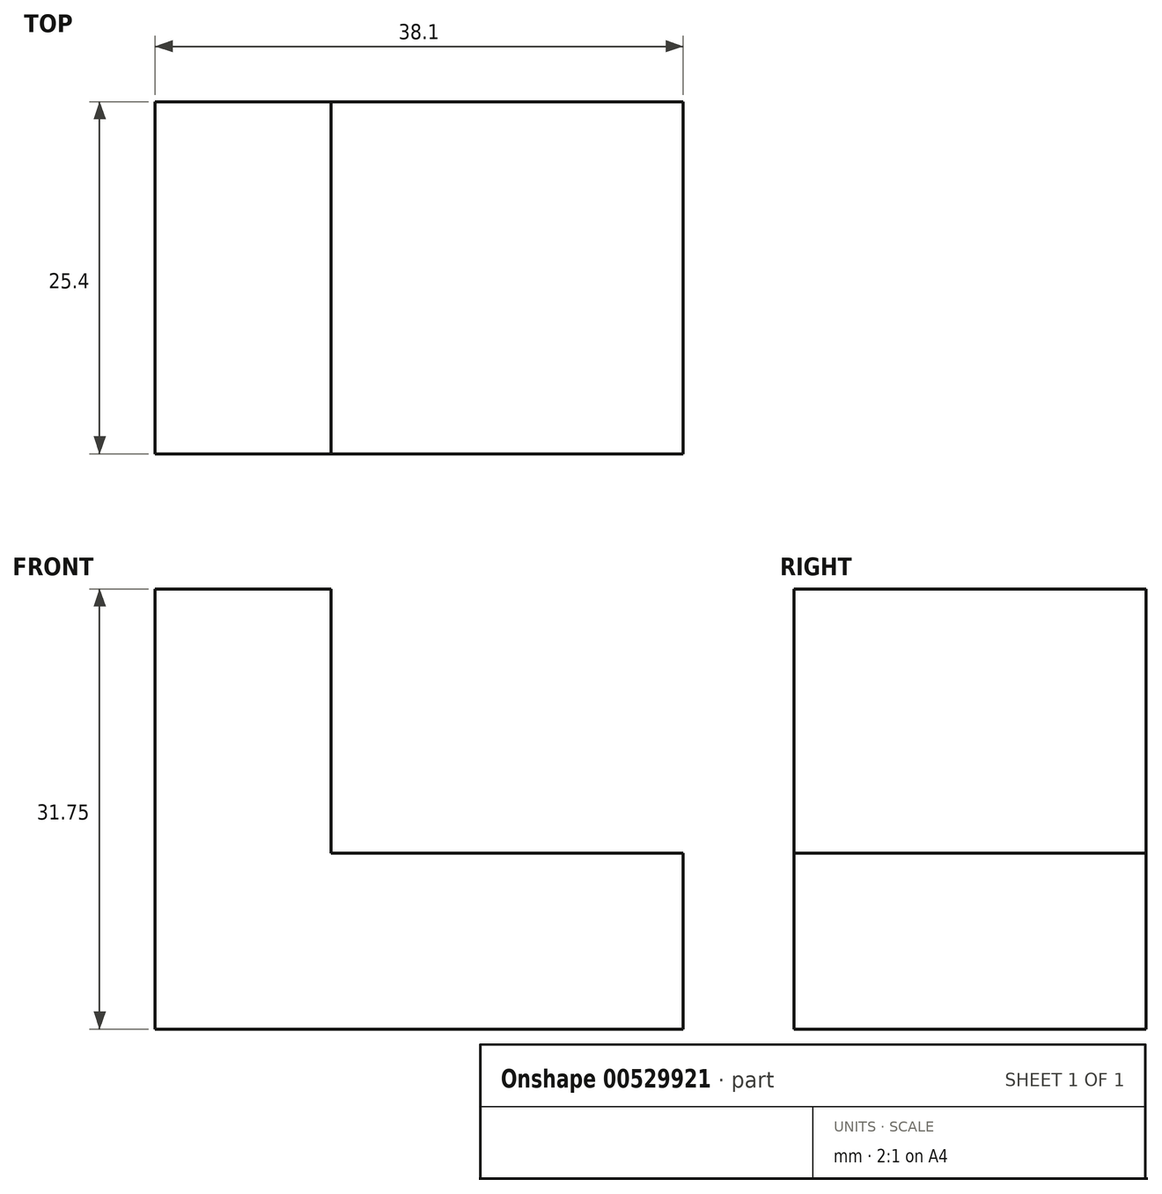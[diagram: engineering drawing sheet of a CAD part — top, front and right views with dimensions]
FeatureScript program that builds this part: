
annotation { "Feature Type Name" : "Feature", "Feature Type Description" : "" }
export const myFeature = defineFeature(function(context is Context, id is Id, definition is map)
    precondition{}
    {
        {
            var Q0;
            Q0=qCreatedBy(makeId("Front.planeOp"),FACE);
            var sketch = newSketch(context, id + "F0", { "sketchPlane" : qUnion([Q0])});
            skLineSegment(sketch, "E0", {"start": v(-54.83, 42.08) * mm, "end": v(-54.83, 10.33) * mm});
            skLineSegment(sketch, "E1", {"start": v(-54.83, 10.33) * mm, "end": v(-16.73, 10.33) * mm});
            skLineSegment(sketch, "E2", {"start": v(-16.73, 10.33) * mm, "end": v(-16.73, 23.03) * mm});
            skLineSegment(sketch, "E3", {"start": v(-16.73, 23.03) * mm, "end": v(-42.13, 23.03) * mm});
            skLineSegment(sketch, "E4", {"start": v(-42.13, 23.03) * mm, "end": v(-42.13, 42.08) * mm});
            skLineSegment(sketch, "E5", {"start": v(-42.13, 42.08) * mm, "end": v(-54.83, 42.08) * mm});
            skSolve(sketch);
        }
        {
            var Q0;
            Q0=makeQuery(id+"F0.imprint","IMPRINT",FACE,{"disambiguationData":[TD([[makeQuery(id+"F0.imprint","IMPRINT",EDGE,{"derivedFrom":sQuery(id+"F0.wireOp",EDGE,"E0")}),1.0]])]});
            extrude(context, id + "F1", {"entities" : qUnion([Q0]), "depth" : 25.4 * mm, "offsetDistance" : 25.4 * mm});
        }
    });
